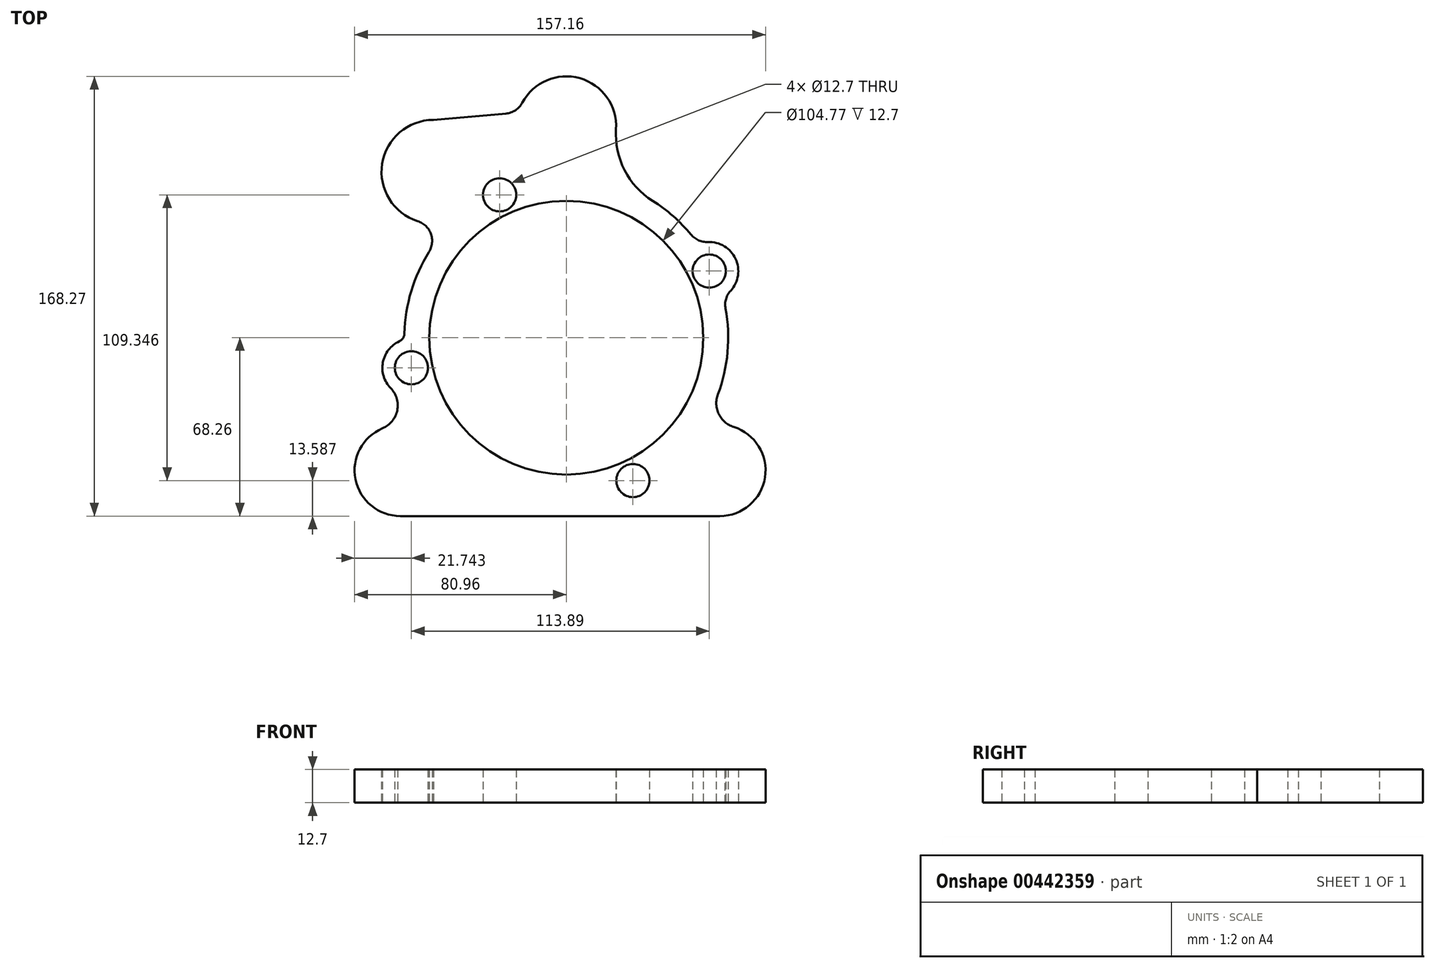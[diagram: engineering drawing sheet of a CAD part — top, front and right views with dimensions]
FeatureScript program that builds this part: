
annotation { "Feature Type Name" : "Feature", "Feature Type Description" : "" }
export const myFeature = defineFeature(function(context is Context, id is Id, definition is map)
    precondition{}
    {
        {
            var Q0;
            Q0=qCreatedBy(makeId("Top.planeOp"),FACE);
            var sketch = newSketch(context, id + "F0", { "sketchPlane" : qUnion([Q0])});
            skCircle(sketch, "E0", {"center": v(0, 0) * mm, "radius": 52.39 * mm});
            skLineSegment(sketch, "E1", {"start": v(0, 0) * mm, "end": v(0, -68.26) * mm, "construction": true});
            skArc(sketch, "E2.0", {"start": v(-61.9, -0.73) * mm, "mid": v(-61.83, -3.2) * mm, "end": v(-61.65, -5.65) * mm});
            skLineSegment(sketch, "E3", {"start": v(0, 0) * mm, "end": v(140.82, 0) * mm, "construction": true});
            skLineSegment(sketch, "E4", {"start": v(0, 0) * mm, "end": v(120.9, 56.38) * mm, "construction": true});
            skCircle(sketch, "E5", {"center": v(0, 0) * mm, "radius": 60.33 * mm, "construction": true});
            skCircle(sketch, "E6", {"center": v(54.67, 25.5) * mm, "radius": 6.35 * mm});
            skLineSegment(sketch, "E7", {"start": v(0, 0) * mm, "end": v(32.57, -69.84) * mm, "construction": true});
            skCircle(sketch, "E8", {"center": v(25.5, -54.67) * mm, "radius": 6.35 * mm});
            skLineSegment(sketch, "E9", {"start": v(0, 0) * mm, "end": v(-28.6, 61.32) * mm, "construction": true});
            skCircle(sketch, "E10", {"center": v(-25.5, 54.67) * mm, "radius": 6.35 * mm});
            skLineSegment(sketch, "E11", {"start": v(0, 0) * mm, "end": v(-71.7, 0) * mm, "construction": true});
            skLineSegment(sketch, "E12", {"start": v(0, 0) * mm, "end": v(-71.37, -13.87) * mm, "construction": true});
            skCircle(sketch, "E13", {"center": v(-59.22, -11.51) * mm, "radius": 6.35 * mm});
            skLineSegment(sketch, "E14", {"start": v(0, -68.26) * mm, "end": v(58.74, -68.26) * mm});
            skLineSegment(sketch, "E15", {"start": v(0, -68.26) * mm, "end": v(-63.5, -68.26) * mm});
            skLineSegment(sketch, "E16", {"start": v(58.74, -68.26) * mm, "end": v(58.74, -50.8) * mm});
            skArc(sketch, "E17", {"start": v(58.74, -68.26) * mm, "mid": v(76, -53.47) * mm, "end": v(64.01, -34.15) * mm});
            skLineSegment(sketch, "E18", {"start": v(-63.5, -68.26) * mm, "end": v(-63.5, -50.8) * mm});
            skArc(sketch, "E19", {"start": v(-70.28, -34.7) * mm, "mid": v(-80.62, -54.26) * mm, "end": v(-63.5, -68.26) * mm});
            skLineSegment(sketch, "E20", {"start": v(-59.22, -11.51) * mm, "end": v(-70.33, -11.51) * mm});
            skArc(sketch, "E21", {"start": v(-57.67, -22.52) * mm, "mid": v(-48.3, -9.4) * mm, "end": v(-61.9, -0.73) * mm});
            skLineSegment(sketch, "E22", {"start": v(57.49, -23.56) * mm, "end": v(66.9, -25.07) * mm});
            skArc(sketch, "E23", {"start": v(57.97, -21.73) * mm, "mid": v(58.33, -29.24) * mm, "end": v(64.01, -34.15) * mm});
            skLineSegment(sketch, "E24", {"start": v(-73.98, -25.93) * mm, "end": v(-64.46, -25.93) * mm});
            skArc(sketch, "E25", {"start": v(-70.28, -34.7) * mm, "mid": v(-64.64, -27.82) * mm, "end": v(-67.17, -19.28) * mm});
            skArc(sketch, "E26", {"start": v(-63.87, -1.42) * mm, "mid": v(-62.45, -0.2) * mm, "end": v(-61.9, 1.58) * mm});
            skArc(sketch, "E27.trimOffspring", {"start": v(-63.87, -1.42) * mm, "mid": v(-70.14, -9.5) * mm, "end": v(-67.17, -19.28) * mm});
            skLineSegment(sketch, "E28", {"start": v(0, 0) * mm, "end": v(0, 63.5) * mm, "construction": true});
            skLineSegment(sketch, "E29", {"start": v(0, 63.5) * mm, "end": v(-50.8, 63.5) * mm});
            skLineSegment(sketch, "E30", {"start": v(-50.8, 63.5) * mm, "end": v(-70.64, 63.5) * mm});
            skArc(sketch, "E31", {"start": v(-50.8, 83.34) * mm, "mid": v(-70.4, 66.55) * mm, "end": v(-56.82, 44.6) * mm});
            skLineSegment(sketch, "E32", {"start": v(-67.17, 37.03) * mm, "end": v(-59.23, 37.03) * mm});
            skArc(sketch, "E33", {"start": v(-52.5, 32.82) * mm, "mid": v(-51.78, 39.76) * mm, "end": v(-56.82, 44.6) * mm});
            skCircle(sketch, "E34", {"center": v(54.67, 25.5) * mm, "radius": 11.11 * mm});
            skLineSegment(sketch, "E35", {"start": v(0, 0) * mm, "end": v(0, 80.96) * mm, "construction": true});
            skLineSegment(sketch, "E36", {"start": v(0, 80.96) * mm, "end": v(-19.05, 80.96) * mm});
            skArc(sketch, "E37", {"start": v(-7.61, 63.5) * mm, "mid": v(18, 87.22) * mm, "end": v(-16.8, 89.93) * mm});
            skLineSegment(sketch, "E38", {"start": v(-50.8, 63.5) * mm, "end": v(-50.8, 83.34) * mm, "construction": true});
            skLineSegment(sketch, "E39", {"start": v(-50.8, 83.34) * mm, "end": v(-21.29, 83.34) * mm, "construction": true});
            skLineSegment(sketch, "E40", {"start": v(-50.8, 83.34) * mm, "end": v(-23.12, 85.77) * mm});
            skLineSegment(sketch, "E41", {"start": v(-23.8, 93.67) * mm, "end": v(-15.87, 93.67) * mm});
            skArc(sketch, "E42", {"start": v(-23.12, 85.77) * mm, "mid": v(-19.43, 87.05) * mm, "end": v(-16.8, 89.93) * mm});
            skLineSegment(sketch, "E43", {"start": v(49.12, 77.88) * mm, "end": v(18.95, 77.88) * mm});
            skArc(sketch, "E44", {"start": v(19.01, 79.77) * mm, "mid": v(22.26, 64.15) * mm, "end": v(33.03, 52.37) * mm});
            skLineSegment(sketch, "E45", {"start": v(53.82, 44.53) * mm, "end": v(61.76, 44.53) * mm});
            skArc(sketch, "E46", {"start": v(47.7, 39.47) * mm, "mid": v(50.6, 37.27) * mm, "end": v(54.18, 36.6) * mm});
            skArc(sketch, "E47.trimOffspring", {"start": v(47.7, 39.47) * mm, "mid": v(-20.23, 58.52) * mm, "end": v(-61.9, 1.58) * mm});
            skArc(sketch, "E48.trimOffspring", {"start": v(57.97, -21.73) * mm, "mid": v(61.4, 7.96) * mm, "end": v(50.51, 35.8) * mm});
            skArc(sketch, "E49.trimOffspring", {"start": v(-60.83, -11.51) * mm, "mid": v(-60.8, -11.66) * mm, "end": v(-60.77, -11.81) * mm});
            skLineSegment(sketch, "E50", {"start": v(-61.9, 1.58) * mm, "end": v(-65.3, 1.67) * mm, "construction": true});
            skSolve(sketch);
        }
        {
            var Q0;
            Q0=makeQuery(id+"F0.imprint","IMPRINT",FACE,{"disambiguationData":[TD([[makeQuery(id+"F0.imprint","IMPRINT",EDGE,{"derivedFrom":sQuery(id+"F0.wireOp",EDGE,"E14")}),1.0]])]});
            var Q1;
            {var subQ10=sQuery(id+"F0.wireOp",EDGE,"E26");Q1=makeQuery(id+"F0.imprint","IMPRINT",FACE,{"disambiguationData":[TD([[makeQuery(id+"F0.imprint","IMPRINT",EDGE,{"derivedFrom":subQ10}),-1.0]])]});}
            var Q2;
            {var subQ4=sQuery(id+"F0.wireOp",EDGE,"E21");var subQ5=sQuery(id+"F0.wireOp",EDGE,"E0");var subQ6=makeQuery(id+"F0.imprint","INTERSECT",VERTEX,{"disambiguationData":[OD(0.0)],"derivedFrom":[subQ5,subQ4]});Q2=makeQuery(id+"F0.imprint","IMPRINT",FACE,{"disambiguationData":[TD([[makeQuery(id+"F0.imprint","IMPRINT",EDGE,{"disambiguationData":[TD([[subQ6,1.0]])],"derivedFrom":subQ5}),-1.0]])]});}
            var Q3;
            {var subQ1=sQuery(id+"F0.wireOp",EDGE,"E30");Q3=makeQuery(id+"F0.imprint","IMPRINT",FACE,{"disambiguationData":[TD([[makeQuery(id+"F0.imprint","IMPRINT",EDGE,{"derivedFrom":subQ1}),-1.0]])]});}
            var Q4;
            {var subQ0=sQuery(id+"F0.wireOp",EDGE,"E44");var subQ5=makeQuery(id+"F0.imprint","IMPRINT",VERTEX,{"derivedFrom":subQ0});Q4=makeQuery(id+"F0.imprint","IMPRINT",FACE,{"disambiguationData":[TD([[makeQuery(id+"F0.imprint","IMPRINT",EDGE,{"disambiguationData":[TD([[subQ5,1.0]])],"derivedFrom":subQ0}),-1.0]])]});}
            var Q5;
            {var subQ1=sQuery(id+"F0.wireOp",EDGE,"E30");Q5=makeQuery(id+"F0.imprint","IMPRINT",FACE,{"disambiguationData":[TD([[makeQuery(id+"F0.imprint","IMPRINT",EDGE,{"derivedFrom":subQ1}),1.0]])]});}
            var Q6;
            {var subQ2=sQuery(id+"F0.wireOp",EDGE,"E48.trimOffspring");var subQ4=sQuery(id+"F0.wireOp",EDGE,"E6");var subQ5=makeQuery(id+"F0.imprint","INTERSECT",VERTEX,{"disambiguationData":[OD(0.0)],"derivedFrom":[subQ4,subQ2]});Q6=makeQuery(id+"F0.imprint","IMPRINT",FACE,{"disambiguationData":[TD([[makeQuery(id+"F0.imprint","IMPRINT",EDGE,{"disambiguationData":[TD([[subQ5,-1.0]])],"derivedFrom":subQ4}),-1.0]])]});}
            var Q7;
            {var subQ1=sQuery(id+"F0.wireOp",EDGE,"E34");var subQ3=sQuery(id+"F0.wireOp",EDGE,"E0");var subQ6=makeQuery(id+"F0.imprint","INTERSECT",VERTEX,{"disambiguationData":[OD(0.0)],"derivedFrom":[subQ3,subQ1]});Q7=makeQuery(id+"F0.imprint","IMPRINT",FACE,{"disambiguationData":[TD([[makeQuery(id+"F0.imprint","IMPRINT",EDGE,{"disambiguationData":[TD([[subQ6,1.0]])],"derivedFrom":subQ3}),-1.0]])]});}
            extrude(context, id + "F1", {"entities" : qUnion([Q0, Q1, Q2, Q3, Q4, Q5, Q6, Q7]), "depth" : 12.7 * mm});
        }
        {
            var Q0;
            Q0=makeQuery(id+"F1.opExtrude","SWEPT_EDGE",EDGE,{"disambiguationData":[OSD([sQuery(id+"F0.wireOp",EDGE,"E34"),sQuery(id+"F0.wireOp",EDGE,"E48.trimOffspring")])]});
            fillet(context, id + "F2", {"entities" : qUnion([Q0]), "radius" : 7.94 * mm, "tangentPropagation" : true, "allowEdgeOverflow" : false});
        }
    });
